# Revit family: Seat-LaZBoy-Kadia_Upholstered_Lounge-KMU30IBC
name_source: partatom
category: Furniture
revit_build: Autodesk Revit 2017 (Build: 20160225_1515(x64)
units: mm (PartAtom-declared; Revit-internal decimal feet)

## family parameters
Always vertical = Yes
Cut with Voids When Loaded = No
OmniClass Number = 23.40.20.00
Room Calculation Point = No
Shared = No
Work Plane-Based = No

## types (4) — shared parameters
Assembly Code = E2020200
Depth = 29.00"
Height = 32.75"
Manufacturer = LaZBoy
Product Documentation Link = URL
URL = https://www.la-z-boy.com
Width = 84.25"

## per-type parameters (varying)
| type | Description | Model | With Armcap |
| Upholstered Arms | 3 Seat Lounge Center Bariatric with Intervening Upholstered Arms | KMU30IBCF | No |
| Urethane Arm Caps | 3 Seat Lounge Center Bariatric with Intervening Urethane Arm Caps | KMU30IBCU | Yes |
| Wood Arm Caps | 3 Seat Lounge Center Bariatric with Intervening Wood Arm Caps | KMU30IBCW | Yes |
| Solid Surface Arm Caps | 3 Seat Lounge Center Bariatric with Intervening Solid Surface Arm Caps | KMU30IBCJ | Yes |

## geometry (parser evidence)
native form markers: Sweep x3
no freeform markers — native parametric forms only
